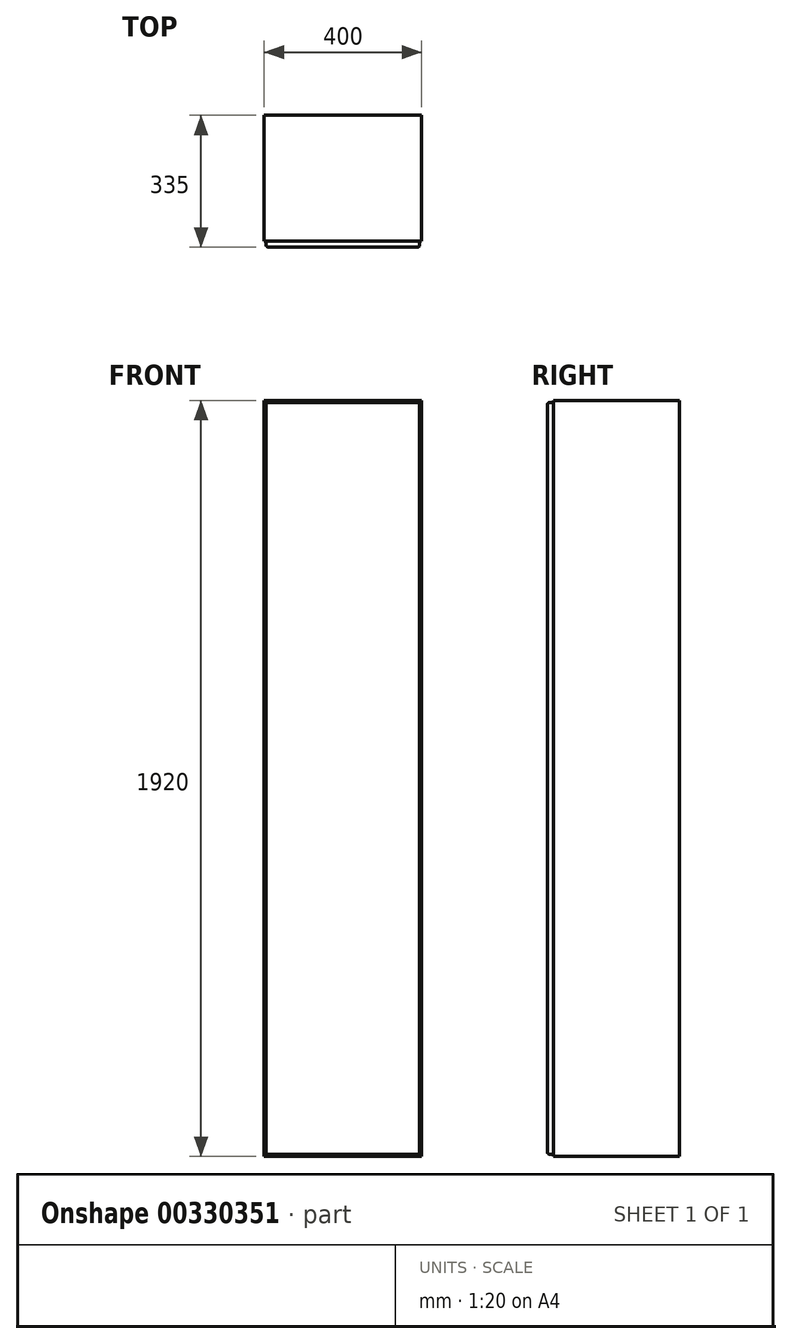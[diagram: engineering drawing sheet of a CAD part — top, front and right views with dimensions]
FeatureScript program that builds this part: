
annotation { "Feature Type Name" : "Feature", "Feature Type Description" : "" }
export const myFeature = defineFeature(function(context is Context, id is Id, definition is map)
    precondition{}
    {
        {
            var Q0;
            Q0=qCreatedBy(makeId("Front.planeOp"),FACE);
            var sketch = newSketch(context, id + "F0", { "sketchPlane" : qUnion([Q0])});
            skLineSegment(sketch, "E0.bottom", {"start": v(0, 0) * mm, "end": v(400, 0) * mm});
            skLineSegment(sketch, "E0.top", {"start": v(0, 1920) * mm, "end": v(400, 1920) * mm});
            skLineSegment(sketch, "E0.left", {"start": v(0, 0) * mm, "end": v(0, 1920) * mm});
            skLineSegment(sketch, "E0.right", {"start": v(400, 0) * mm, "end": v(400, 1920) * mm});
            skSolve(sketch);
        }
        {
            var Q0;
            Q0=qSketchRegion(id+"F0",true);
            extrude(context, id + "F1", {"entities" : qUnion([Q0]), "offsetDistance" : 25 * mm, "depth" : 320 * mm});
        }
        {
            var Q0;
            Q0=makeQuery(id+"F1.opExtrude","CAP_FACE",FACE,{"disambiguationData":[OSD([sQuery(id+"F0.wireOp",EDGE,"E0.bottom"),sQuery(id+"F0.wireOp",EDGE,"E0.top"),sQuery(id+"F0.wireOp",EDGE,"E0.left"),sQuery(id+"F0.wireOp",EDGE,"E0.right")])],"isStart":false});
            var sketch = newSketch(context, id + "F2", { "sketchPlane" : qUnion([Q0])});
            skLineSegment(sketch, "E1.0", {"start": v(395, 1915) * mm, "end": v(5, 1915) * mm});
            skLineSegment(sketch, "E1.1", {"start": v(395, 5) * mm, "end": v(395, 1915) * mm});
            skLineSegment(sketch, "E1.2", {"start": v(5, 5) * mm, "end": v(395, 5) * mm});
            skLineSegment(sketch, "E1.3", {"start": v(5, 1915) * mm, "end": v(5, 5) * mm});
            skSolve(sketch);
        }
        {
            var Q0;
            Q0 = qSketchRegion(id + "F2", true);
            extrude(context, id + "F3", {"entities" : qUnion([Q0]), "operationType" : NewBodyOperationType.ADD, "depth" : 15 * mm, "offsetDistance" : 25 * mm});
        }
        {
            var Q0;
            Q0=makeQuery(id+"F3.opExtrude","CAP_FACE",FACE,{"disambiguationData":[OSD([sQuery(id+"F2.wireOp",EDGE,"E1.0"),sQuery(id+"F2.wireOp",EDGE,"E1.1"),sQuery(id+"F2.wireOp",EDGE,"E1.2"),sQuery(id+"F2.wireOp",EDGE,"E1.3")])],"isStart":false});
            var Q1;
            Q1=makeQuery(id+"F3.opExtrude","SWEPT_EDGE",EDGE,{"disambiguationData":[OSD([sQuery(id+"F2.wireOp",EDGE,"E1.0"),sQuery(id+"F2.wireOp",EDGE,"E1.1")])]});
            var Q2;
            Q2=makeQuery(id+"F3.opExtrude","SWEPT_EDGE",EDGE,{"disambiguationData":[OSD([sQuery(id+"F2.wireOp",EDGE,"E1.0"),sQuery(id+"F2.wireOp",EDGE,"E1.3")])]});
            var Q3;
            Q3=makeQuery(id+"F3.opExtrude","SWEPT_EDGE",EDGE,{"disambiguationData":[OSD([sQuery(id+"F2.wireOp",EDGE,"E1.1"),sQuery(id+"F2.wireOp",EDGE,"E1.2")])]});
            var Q4;
            Q4=makeQuery(id+"F3.opExtrude","SWEPT_EDGE",EDGE,{"disambiguationData":[OSD([sQuery(id+"F2.wireOp",EDGE,"E1.2"),sQuery(id+"F2.wireOp",EDGE,"E1.3")])]});
            fillet(context, id + "F4", {"entities" : qUnion([Q0, Q1, Q2, Q3, Q4]), "radius" : 5 * mm, "tangentPropagation" : true, "allowEdgeOverflow" : false});
        }
    });
